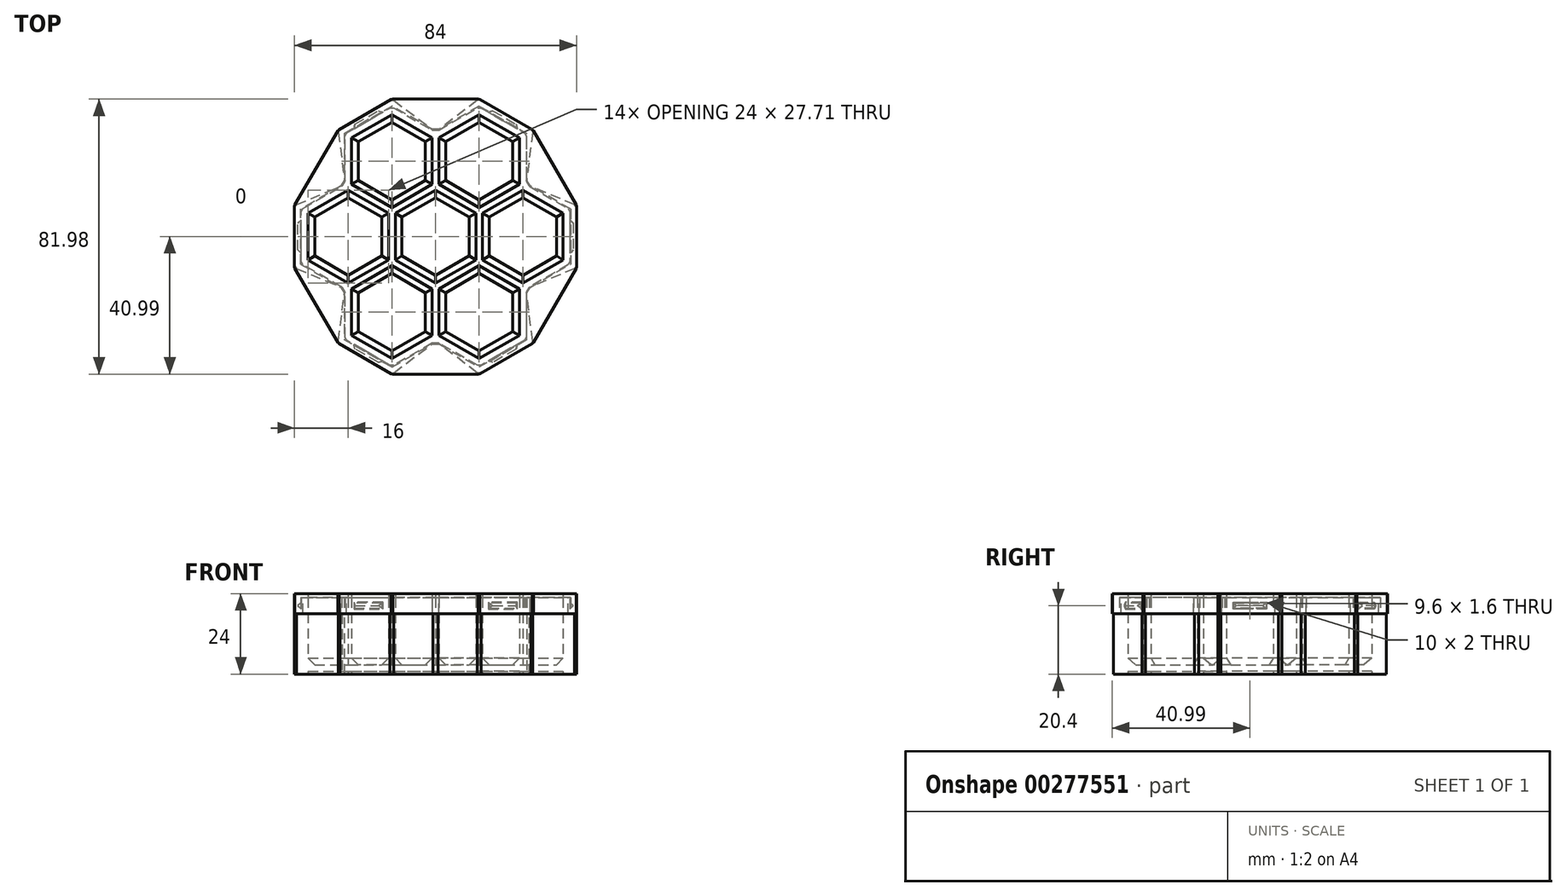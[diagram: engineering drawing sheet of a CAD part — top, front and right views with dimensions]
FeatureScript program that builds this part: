
annotation { "Feature Type Name" : "Feature", "Feature Type Description" : "" }
export const myFeature = defineFeature(function(context is Context, id is Id, definition is map)
    precondition{}
    {
        {
            assignVariable(context, id + "F0", {"name" : "BOX_HEIGHT", "anyValue" : 24});
        }
        {
            assignVariable(context, id + "F1", {"name" : "DICE_HEIGHT", "anyValue" : 20});
        }
        {
            assignVariable(context, id + "F2", {"name" : "LID_THICNESS", "anyValue" : 1.2});
        }
        {
            assignVariable(context, id + "F3", {"name" : "LID_HEIGHT", "anyValue" : 6});
        }
        {
            assignVariable(context, id + "F4", {"name" : "WALL_THICNESS", "anyValue" : 2});
        }
        {
            assignVariable(context, id + "F5", {"name" : "WALL_OVERLAP", "anyValue" : 2});
        }
        {
            var Q0;
            Q0=qCreatedBy(makeId("Top.planeOp"),FACE);
            var sketch = newSketch(context, id + "F6", { "sketchPlane" : qUnion([Q0])});
            skCircle(sketch, "E0.cCircle", {"center": v(0, 0) * mm, "radius": 12 * mm, "construction": true});
            skLineSegment(sketch, "E0.0", {"start": v(12, 6.93) * mm, "end": v(12, -6.93) * mm});
            skLineSegment(sketch, "E0.1", {"start": v(12, -6.93) * mm, "end": v(0, -13.86) * mm});
            skLineSegment(sketch, "E0.2", {"start": v(0, -13.86) * mm, "end": v(-12, -6.93) * mm});
            skLineSegment(sketch, "E0.3", {"start": v(-12, -6.93) * mm, "end": v(-12, 6.93) * mm});
            skLineSegment(sketch, "E0.4", {"start": v(-12, 6.93) * mm, "end": v(0, 13.86) * mm});
            skLineSegment(sketch, "E0.5", {"start": v(0, 13.86) * mm, "end": v(12, 6.93) * mm});
            skPoint(sketch, "E0.0.midPoint", {"position": v(12, 0) * mm});
            skSolve(sketch);
        }
        {
            var Q0;
            Q0=qCreatedBy(makeId("Top.planeOp"),FACE);
            var sketch = newSketch(context, id + "F7", { "sketchPlane" : qUnion([Q0])});
            skCircle(sketch, "E1.cCircle", {"center": v(26, 0) * mm, "radius": 12 * mm, "construction": true});
            skLineSegment(sketch, "E1.0", {"start": v(38, 6.93) * mm, "end": v(38, -6.93) * mm});
            skLineSegment(sketch, "E1.1", {"start": v(38, -6.93) * mm, "end": v(26, -13.86) * mm});
            skLineSegment(sketch, "E1.2", {"start": v(26, -13.86) * mm, "end": v(14, -6.93) * mm});
            skLineSegment(sketch, "E1.3", {"start": v(14, -6.93) * mm, "end": v(14, 6.93) * mm});
            skLineSegment(sketch, "E1.4", {"start": v(14, 6.93) * mm, "end": v(26, 13.86) * mm});
            skLineSegment(sketch, "E1.5", {"start": v(26, 13.86) * mm, "end": v(38, 6.93) * mm});
            skPoint(sketch, "E1.0.midPoint", {"position": v(38, 0) * mm});
            skLineSegment(sketch, "E2.1.0", {"start": v(13, 8.66) * mm, "end": v(1, 15.59) * mm});
            skLineSegment(sketch, "E2.1.1", {"start": v(1, 15.59) * mm, "end": v(1, 29.44) * mm});
            skLineSegment(sketch, "E2.1.2", {"start": v(1, 29.44) * mm, "end": v(13, 36.37) * mm});
            skLineSegment(sketch, "E2.1.3", {"start": v(13, 36.37) * mm, "end": v(25, 29.44) * mm});
            skPoint(sketch, "E2.1.4", {"position": v(19, 32.9) * mm});
            skLineSegment(sketch, "E2.1.5", {"start": v(25, 29.44) * mm, "end": v(25, 15.59) * mm});
            skLineSegment(sketch, "E2.1.6", {"start": v(25, 15.59) * mm, "end": v(13, 8.66) * mm});
            skLineSegment(sketch, "E2.2.0", {"start": v(-1, 15.59) * mm, "end": v(-13, 8.66) * mm});
            skLineSegment(sketch, "E2.2.1", {"start": v(-13, 8.66) * mm, "end": v(-25, 15.59) * mm});
            skLineSegment(sketch, "E2.2.2", {"start": v(-25, 15.59) * mm, "end": v(-25, 29.44) * mm});
            skLineSegment(sketch, "E2.2.3", {"start": v(-25, 29.44) * mm, "end": v(-13, 36.37) * mm});
            skPoint(sketch, "E2.2.4", {"position": v(-19, 32.9) * mm});
            skLineSegment(sketch, "E2.2.5", {"start": v(-13, 36.37) * mm, "end": v(-1, 29.44) * mm});
            skLineSegment(sketch, "E2.2.6", {"start": v(-1, 29.44) * mm, "end": v(-1, 15.59) * mm});
            skLineSegment(sketch, "E2.3.0", {"start": v(-14, 6.93) * mm, "end": v(-14, -6.93) * mm});
            skLineSegment(sketch, "E2.3.1", {"start": v(-14, -6.93) * mm, "end": v(-26, -13.86) * mm});
            skLineSegment(sketch, "E2.3.2", {"start": v(-26, -13.86) * mm, "end": v(-38, -6.93) * mm});
            skLineSegment(sketch, "E2.3.3", {"start": v(-38, -6.93) * mm, "end": v(-38, 6.93) * mm});
            skPoint(sketch, "E2.3.4", {"position": v(-38, 0) * mm});
            skLineSegment(sketch, "E2.3.5", {"start": v(-38, 6.93) * mm, "end": v(-26, 13.86) * mm});
            skLineSegment(sketch, "E2.3.6", {"start": v(-26, 13.86) * mm, "end": v(-14, 6.93) * mm});
            skLineSegment(sketch, "E2.4.0", {"start": v(-13, -8.66) * mm, "end": v(-1, -15.59) * mm});
            skLineSegment(sketch, "E2.4.1", {"start": v(-1, -15.59) * mm, "end": v(-1, -29.44) * mm});
            skLineSegment(sketch, "E2.4.2", {"start": v(-1, -29.44) * mm, "end": v(-13, -36.37) * mm});
            skLineSegment(sketch, "E2.4.3", {"start": v(-13, -36.37) * mm, "end": v(-25, -29.44) * mm});
            skPoint(sketch, "E2.4.4", {"position": v(-19, -32.9) * mm});
            skLineSegment(sketch, "E2.4.5", {"start": v(-25, -29.44) * mm, "end": v(-25, -15.59) * mm});
            skLineSegment(sketch, "E2.4.6", {"start": v(-25, -15.59) * mm, "end": v(-13, -8.66) * mm});
            skLineSegment(sketch, "E2.5.0", {"start": v(1, -15.59) * mm, "end": v(13, -8.66) * mm});
            skLineSegment(sketch, "E2.5.1", {"start": v(13, -8.66) * mm, "end": v(25, -15.59) * mm});
            skLineSegment(sketch, "E2.5.2", {"start": v(25, -15.59) * mm, "end": v(25, -29.44) * mm});
            skLineSegment(sketch, "E2.5.3", {"start": v(25, -29.44) * mm, "end": v(13, -36.37) * mm});
            skPoint(sketch, "E2.5.4", {"position": v(19, -32.9) * mm});
            skLineSegment(sketch, "E2.5.5", {"start": v(13, -36.37) * mm, "end": v(1, -29.44) * mm});
            skLineSegment(sketch, "E2.5.6", {"start": v(1, -29.44) * mm, "end": v(1, -15.59) * mm});
            skPoint(sketch, "E2.center", {"position": v(0, 0) * mm});
            skSolve(sketch);
        }
        {
            var Q0;
            Q0=qCreatedBy(makeId("Top.planeOp"),FACE);
            var sketch = newSketch(context, id + "F8", { "sketchPlane" : qUnion([Q0])});
            skLineSegment(sketch, "E3.0", {"start": v(-40, 8.08) * mm, "end": v(-27, 15.59) * mm});
            skLineSegment(sketch, "E3.1", {"start": v(-40, -8.08) * mm, "end": v(-40, 8.08) * mm});
            skLineSegment(sketch, "E3.2", {"start": v(-27, -15.59) * mm, "end": v(-40, -8.08) * mm});
            skLineSegment(sketch, "E4", {"start": v(-27, -15.59) * mm, "end": v(-12, -6.93) * mm, "construction": true});
            skLineSegment(sketch, "E5", {"start": v(-27, 15.59) * mm, "end": v(-12, 6.93) * mm, "construction": true});
            skLineSegment(sketch, "E6.1.0", {"start": v(0, -31.18) * mm, "end": v(-13, -38.68) * mm});
            skLineSegment(sketch, "E6.1.1", {"start": v(-13, -38.68) * mm, "end": v(-27, -30.6) * mm});
            skLineSegment(sketch, "E6.1.2", {"start": v(-27, -30.6) * mm, "end": v(-27, -15.59) * mm});
            skLineSegment(sketch, "E6.2.0", {"start": v(27, -15.59) * mm, "end": v(27, -30.6) * mm});
            skLineSegment(sketch, "E6.2.1", {"start": v(27, -30.6) * mm, "end": v(13, -38.68) * mm});
            skLineSegment(sketch, "E6.2.2", {"start": v(13, -38.68) * mm, "end": v(0, -31.18) * mm});
            skLineSegment(sketch, "E6.3.0", {"start": v(27, 15.59) * mm, "end": v(40, 8.08) * mm});
            skLineSegment(sketch, "E6.3.1", {"start": v(40, 8.08) * mm, "end": v(40, -8.08) * mm});
            skLineSegment(sketch, "E6.3.2", {"start": v(40, -8.08) * mm, "end": v(27, -15.59) * mm});
            skLineSegment(sketch, "E6.4.0", {"start": v(0, 31.18) * mm, "end": v(13, 38.68) * mm});
            skLineSegment(sketch, "E6.4.1", {"start": v(13, 38.68) * mm, "end": v(27, 30.6) * mm});
            skLineSegment(sketch, "E6.4.2", {"start": v(27, 30.6) * mm, "end": v(27, 15.59) * mm});
            skLineSegment(sketch, "E6.5.0", {"start": v(-27, 15.59) * mm, "end": v(-27, 30.6) * mm});
            skLineSegment(sketch, "E6.5.1", {"start": v(-27, 30.6) * mm, "end": v(-13, 38.68) * mm});
            skLineSegment(sketch, "E6.5.2", {"start": v(-13, 38.68) * mm, "end": v(0, 31.18) * mm});
            skPoint(sketch, "E6.center", {"position": v(0, 0) * mm});
            skSolve(sketch);
        }
        {
            var Q0;
            Q0=qCreatedBy(makeId("Top.planeOp"),FACE);
            var sketch = newSketch(context, id + "F9", { "sketchPlane" : qUnion([Q0])});
            skLineSegment(sketch, "E7.0", {"start": v(-42, -9.24) * mm, "end": v(-42, 9.24) * mm});
            skLineSegment(sketch, "E8", {"start": v(-42, 9.24) * mm, "end": v(-38, 6.93) * mm, "construction": true});
            skLineSegment(sketch, "E9", {"start": v(-42, -9.24) * mm, "end": v(-38, -6.93) * mm, "construction": true});
            skLineSegment(sketch, "E10", {"start": v(-42, -9.24) * mm, "end": v(-27, -15.59) * mm});
            skLineSegment(sketch, "E11", {"start": v(-42, 9.24) * mm, "end": v(-27, 15.59) * mm});
            skLineSegment(sketch, "E12.1.0", {"start": v(-13, -41) * mm, "end": v(0, -31.18) * mm});
            skLineSegment(sketch, "E12.1.1", {"start": v(-13, -41) * mm, "end": v(-29, -31.75) * mm});
            skLineSegment(sketch, "E12.1.2", {"start": v(-29, -31.75) * mm, "end": v(-27, -15.59) * mm});
            skLineSegment(sketch, "E12.2.0", {"start": v(29, -31.75) * mm, "end": v(27, -15.59) * mm});
            skLineSegment(sketch, "E12.2.1", {"start": v(29, -31.75) * mm, "end": v(13, -41) * mm});
            skLineSegment(sketch, "E12.2.2", {"start": v(13, -41) * mm, "end": v(0, -31.18) * mm});
            skLineSegment(sketch, "E12.3.0", {"start": v(42, 9.24) * mm, "end": v(27, 15.59) * mm});
            skLineSegment(sketch, "E12.3.1", {"start": v(42, 9.24) * mm, "end": v(42, -9.24) * mm});
            skLineSegment(sketch, "E12.3.2", {"start": v(42, -9.24) * mm, "end": v(27, -15.59) * mm});
            skLineSegment(sketch, "E12.4.0", {"start": v(13, 41) * mm, "end": v(0, 31.18) * mm});
            skLineSegment(sketch, "E12.4.1", {"start": v(13, 41) * mm, "end": v(29, 31.75) * mm});
            skLineSegment(sketch, "E12.4.2", {"start": v(29, 31.75) * mm, "end": v(27, 15.59) * mm});
            skLineSegment(sketch, "E12.5.0", {"start": v(-29, 31.75) * mm, "end": v(-27, 15.59) * mm});
            skLineSegment(sketch, "E12.5.1", {"start": v(-29, 31.75) * mm, "end": v(-13, 41) * mm});
            skLineSegment(sketch, "E12.5.2", {"start": v(-13, 41) * mm, "end": v(0, 31.18) * mm});
            skPoint(sketch, "E12.center", {"position": v(0, 0) * mm});
            skLineSegment(sketch, "E13", {"start": v(-29, 31.75) * mm, "end": v(-42, 9.24) * mm});
            skLineSegment(sketch, "E14", {"start": v(-42, -9.24) * mm, "end": v(-29, -31.75) * mm});
            skLineSegment(sketch, "E15", {"start": v(-13, -41) * mm, "end": v(13, -41) * mm});
            skLineSegment(sketch, "E16", {"start": v(29, -31.75) * mm, "end": v(42, -9.24) * mm});
            skLineSegment(sketch, "E17", {"start": v(42, 9.24) * mm, "end": v(29, 31.75) * mm});
            skLineSegment(sketch, "E18", {"start": v(13, 41) * mm, "end": v(-13, 41) * mm});
            skSolve(sketch);
        }
        {
            var Q0;
            Q0=makeQuery(id+"F8.imprint","IMPRINT",FACE,{"disambiguationData":[TD([[makeQuery(id+"F8.imprint","IMPRINT",EDGE,{"derivedFrom":sQuery(id+"F8.wireOp",EDGE,"E3.0")}),-1.0]])]});
            extrude(context, id + "F10", {"entities" : qUnion([Q0]), "depth" : (getVariable(context, 'BOX_HEIGHT') - getVariable(context, 'LID_THICNESS')) * mm});
        }
        {
            var Q0;
            Q0=makeQuery(id+"F9.imprint","IMPRINT",FACE,{"disambiguationData":[TD([[makeQuery(id+"F9.imprint","IMPRINT",EDGE,{"derivedFrom":sQuery(id+"F9.wireOp",EDGE,"E7.0")}),-1.0]])]});
            extrude(context, id + "F11", {"entities" : qUnion([Q0]), "operationType" : NewBodyOperationType.ADD, "depth" : (getVariable(context, 'BOX_HEIGHT') - getVariable(context, 'LID_HEIGHT')) * mm});
        }
        {
            var Q0;
            Q0=makeQuery(id+"F10.opExtrude","SWEPT_FACE",FACE,{"disambiguationData":[OSD([sQuery(id+"F8.wireOp",EDGE,"E6.3.1")])]});
            var sketch = newSketch(context, id + "F12", { "sketchPlane" : qUnion([Q0])});
            skLineSegment(sketch, "E19.bottom", {"start": v(5, 21.4) * mm, "end": v(-5, 21.4) * mm});
            skLineSegment(sketch, "E19.top", {"start": v(5, 19.4) * mm, "end": v(-5, 19.4) * mm});
            skLineSegment(sketch, "E19.left", {"start": v(5, 21.4) * mm, "end": v(5, 19.4) * mm});
            skLineSegment(sketch, "E19.right", {"start": v(-5, 21.4) * mm, "end": v(-5, 19.4) * mm});
            skPoint(sketch, "E19.middle", {"position": v(0, 20.4) * mm});
            skPoint(sketch, "E19.middle.positionSnap0", {"position": v(-8.08, 20.4) * mm});
            skPoint(sketch, "E19.centerSnap0", {"position": v(-8.08, 20.4) * mm});
            skSolve(sketch);
        }
        {
            var Q0;
            Q0=makeQuery(id+"F12.imprint","IMPRINT",FACE,{"disambiguationData":[TD([[makeQuery(id+"F12.imprint","IMPRINT",EDGE,{"derivedFrom":sQuery(id+"F12.wireOp",EDGE,"E19.bottom")}),1.0]])]});
            extrude(context, id + "F13", {"entities" : qUnion([Q0]), "depth" : 25 * mm, "hasDraft" : true, "draftAngle" : 45 * degree, "draftPullDirection" : true});
        }
        {
            var Q0;
            Q0=qCreatedBy(makeId("Front.planeOp"),FACE);
            var sketch = newSketch(context, id + "F14", { "sketchPlane" : qUnion([Q0])});
            skLineSegment(sketch, "E20", {"start": v(0, 0) * mm, "end": v(0, 24) * mm, "construction": true});
            skSolve(sketch);
        }
        {
            var Q0;
            Q0=makeQuery(id+"F13.opExtrude","SWEPT_BODY",BODY,{"disambiguationData":[OSD([sQuery(id+"F12.wireOp",EDGE,"E19.bottom"),sQuery(id+"F12.wireOp",EDGE,"E19.top"),sQuery(id+"F12.wireOp",EDGE,"E19.left"),sQuery(id+"F12.wireOp",EDGE,"E19.right")])]});
            var Q1;
            Q1=sQuery(id+"F14.wireOp",EDGE,"E20");
            circularPattern(context, id + "F15", {"operationType" : NewBodyOperationType.ADD, "entities" : qUnion([Q0]), "axis" : qUnion([Q1]), "angle" : 360 * degree, "instanceCount" : 6, "equalSpace" : true});
        }
        {
            var Q0;
            Q0=makeQuery(id+"F10.opExtrude","SWEPT_EDGE",EDGE,{"disambiguationData":[OSD([sQuery(id+"F8.wireOp",EDGE,"E6.3.0"),sQuery(id+"F8.wireOp",EDGE,"E6.4.2")])]});
            var Q1;
            Q1=makeQuery(id+"F10.opExtrude","SWEPT_EDGE",EDGE,{"disambiguationData":[OSD([sQuery(id+"F8.wireOp",EDGE,"E6.4.0"),sQuery(id+"F8.wireOp",EDGE,"E6.5.2")])]});
            var Q2;
            Q2=makeQuery(id+"F10.opExtrude","SWEPT_EDGE",EDGE,{"disambiguationData":[OSD([sQuery(id+"F8.wireOp",EDGE,"E3.0"),sQuery(id+"F8.wireOp",EDGE,"E6.5.0")])]});
            var Q3;
            Q3=makeQuery(id+"F10.opExtrude","SWEPT_EDGE",EDGE,{"disambiguationData":[OSD([sQuery(id+"F8.wireOp",EDGE,"E3.2"),sQuery(id+"F8.wireOp",EDGE,"E6.1.2")])]});
            var Q4;
            Q4=makeQuery(id+"F10.opExtrude","SWEPT_EDGE",EDGE,{"disambiguationData":[OSD([sQuery(id+"F8.wireOp",EDGE,"E6.1.0"),sQuery(id+"F8.wireOp",EDGE,"E6.2.2")])]});
            var Q5;
            Q5=makeQuery(id+"F10.opExtrude","SWEPT_EDGE",EDGE,{"disambiguationData":[OSD([sQuery(id+"F8.wireOp",EDGE,"E6.2.0"),sQuery(id+"F8.wireOp",EDGE,"E6.3.2")])]});
            chamfer(context, id + "F16", {"entities" : qUnion([Q0, Q1, Q2, Q3, Q4, Q5]), "width" : (getVariable(context, 'WALL_THICNESS')) * mm, "tangentPropagation" : true});
        }
        {
            var Q0;
            Q0=makeQuery(id+"F9.imprint","IMPRINT",FACE,{"disambiguationData":[TD([[makeQuery(id+"F9.imprint","IMPRINT",EDGE,{"derivedFrom":sQuery(id+"F9.wireOp",EDGE,"E7.0")}),-1.0]])]});
            var Q1;
            Q1=makeQuery(id+"F9.imprint","IMPRINT",FACE,{"disambiguationData":[TD([[makeQuery(id+"F9.imprint","IMPRINT",EDGE,{"derivedFrom":sQuery(id+"F9.wireOp",EDGE,"E11")}),1.0]])]});
            var Q2;
            Q2=makeQuery(id+"F9.imprint","IMPRINT",FACE,{"disambiguationData":[TD([[makeQuery(id+"F9.imprint","IMPRINT",EDGE,{"derivedFrom":sQuery(id+"F9.wireOp",EDGE,"E10")}),-1.0]])]});
            var Q3;
            Q3=makeQuery(id+"F9.imprint","IMPRINT",FACE,{"disambiguationData":[TD([[makeQuery(id+"F9.imprint","IMPRINT",EDGE,{"derivedFrom":sQuery(id+"F9.wireOp",EDGE,"E12.1.0")}),-1.0]])]});
            var Q4;
            Q4=makeQuery(id+"F9.imprint","IMPRINT",FACE,{"disambiguationData":[TD([[makeQuery(id+"F9.imprint","IMPRINT",EDGE,{"derivedFrom":sQuery(id+"F9.wireOp",EDGE,"E12.2.0")}),-1.0]])]});
            var Q5;
            Q5=makeQuery(id+"F9.imprint","IMPRINT",FACE,{"disambiguationData":[TD([[makeQuery(id+"F9.imprint","IMPRINT",EDGE,{"derivedFrom":sQuery(id+"F9.wireOp",EDGE,"E12.3.0")}),-1.0]])]});
            var Q6;
            Q6=makeQuery(id+"F9.imprint","IMPRINT",FACE,{"disambiguationData":[TD([[makeQuery(id+"F9.imprint","IMPRINT",EDGE,{"derivedFrom":sQuery(id+"F9.wireOp",EDGE,"E12.4.0")}),-1.0]])]});
            extrude(context, id + "F17", {"entities" : qUnion([Q0, Q1, Q2, Q3, Q4, Q5, Q6]), "depth" : (getVariable(context, 'BOX_HEIGHT')) * mm, "hasSecondDirection" : true, "secondDirectionOppositeDirection" : false, "secondDirectionDepth" : (getVariable(context, 'BOX_HEIGHT') - getVariable(context, 'LID_HEIGHT')) * mm});
        }
        {
            var Q0;
            Q0=makeQuery(id+"F10.opExtrude","SWEPT_BODY",BODY,{"disambiguationData":[OSD([sQuery(id+"F8.wireOp",EDGE,"E3.0"),sQuery(id+"F8.wireOp",EDGE,"E3.1"),sQuery(id+"F8.wireOp",EDGE,"E3.2"),sQuery(id+"F8.wireOp",EDGE,"E6.1.0"),sQuery(id+"F8.wireOp",EDGE,"E6.1.1"),sQuery(id+"F8.wireOp",EDGE,"E6.1.2"),sQuery(id+"F8.wireOp",EDGE,"E6.2.0"),sQuery(id+"F8.wireOp",EDGE,"E6.2.1"),sQuery(id+"F8.wireOp",EDGE,"E6.2.2"),sQuery(id+"F8.wireOp",EDGE,"E6.3.0"),sQuery(id+"F8.wireOp",EDGE,"E6.3.1"),sQuery(id+"F8.wireOp",EDGE,"E6.3.2"),sQuery(id+"F8.wireOp",EDGE,"E6.4.0"),sQuery(id+"F8.wireOp",EDGE,"E6.4.1"),sQuery(id+"F8.wireOp",EDGE,"E6.4.2"),sQuery(id+"F8.wireOp",EDGE,"E6.5.0"),sQuery(id+"F8.wireOp",EDGE,"E6.5.1"),sQuery(id+"F8.wireOp",EDGE,"E6.5.2")])]});
            var Q1;
            Q1=makeQuery(id+"F17.opExtrude","SWEPT_BODY",BODY,{"disambiguationData":[OSD([sQuery(id+"F9.wireOp",EDGE,"E7.0"),sQuery(id+"F9.wireOp",EDGE,"E12.1.1"),sQuery(id+"F9.wireOp",EDGE,"E12.2.1"),sQuery(id+"F9.wireOp",EDGE,"E12.3.1"),sQuery(id+"F9.wireOp",EDGE,"E12.4.1"),sQuery(id+"F9.wireOp",EDGE,"E12.5.1"),sQuery(id+"F9.wireOp",EDGE,"E13"),sQuery(id+"F9.wireOp",EDGE,"E14"),sQuery(id+"F9.wireOp",EDGE,"E15"),sQuery(id+"F9.wireOp",EDGE,"E16"),sQuery(id+"F9.wireOp",EDGE,"E17"),sQuery(id+"F9.wireOp",EDGE,"E18")])]});
            var Q2;
            Q2=makeQuery(id+"F10.opExtrude","SWEPT_FACE",FACE,{"disambiguationData":[OSD([sQuery(id+"F8.wireOp",EDGE,"E6.3.0")])]});
            var Q3;
            Q3=makeQuery(id+"F16.opChamfer","BLEND_FACE",FACE,{"disambiguationData":[OSD([sQuery(id+"F8.wireOp",EDGE,"E6.3.0"),sQuery(id+"F8.wireOp",EDGE,"E6.4.2")])]});
            var Q4;
            Q4=makeQuery(id+"F10.opExtrude","SWEPT_FACE",FACE,{"disambiguationData":[OSD([sQuery(id+"F8.wireOp",EDGE,"E6.4.2")])]});
            var Q5;
            Q5=makeQuery(id+"F10.opExtrude","SWEPT_FACE",FACE,{"disambiguationData":[OSD([sQuery(id+"F8.wireOp",EDGE,"E6.4.1")])]});
            var Q6;
            Q6=makeQuery(id+"F10.opExtrude","SWEPT_FACE",FACE,{"disambiguationData":[OSD([sQuery(id+"F8.wireOp",EDGE,"E6.4.0")])]});
            var Q7;
            Q7=makeQuery(id+"F16.opChamfer","BLEND_FACE",FACE,{"disambiguationData":[OSD([sQuery(id+"F8.wireOp",EDGE,"E6.4.0"),sQuery(id+"F8.wireOp",EDGE,"E6.5.2")])]});
            var Q8;
            Q8=makeQuery(id+"F10.opExtrude","SWEPT_FACE",FACE,{"disambiguationData":[OSD([sQuery(id+"F8.wireOp",EDGE,"E6.5.2")])]});
            var Q9;
            Q9=makeQuery(id+"F10.opExtrude","SWEPT_FACE",FACE,{"disambiguationData":[OSD([sQuery(id+"F8.wireOp",EDGE,"E6.5.1")])]});
            var Q10;
            Q10=makeQuery(id+"F10.opExtrude","SWEPT_FACE",FACE,{"disambiguationData":[OSD([sQuery(id+"F8.wireOp",EDGE,"E6.5.0")])]});
            var Q11;
            Q11=makeQuery(id+"F16.opChamfer","BLEND_FACE",FACE,{"disambiguationData":[OSD([sQuery(id+"F8.wireOp",EDGE,"E3.0"),sQuery(id+"F8.wireOp",EDGE,"E6.5.0")])]});
            var Q12;
            Q12=makeQuery(id+"F10.opExtrude","SWEPT_FACE",FACE,{"disambiguationData":[OSD([sQuery(id+"F8.wireOp",EDGE,"E3.0")])]});
            var Q13;
            Q13=makeQuery(id+"F10.opExtrude","SWEPT_FACE",FACE,{"disambiguationData":[OSD([sQuery(id+"F8.wireOp",EDGE,"E3.1")])]});
            var Q14;
            Q14=makeQuery(id+"F10.opExtrude","SWEPT_FACE",FACE,{"disambiguationData":[OSD([sQuery(id+"F8.wireOp",EDGE,"E3.2")])]});
            var Q15;
            Q15=makeQuery(id+"F16.opChamfer","BLEND_FACE",FACE,{"disambiguationData":[OSD([sQuery(id+"F8.wireOp",EDGE,"E3.2"),sQuery(id+"F8.wireOp",EDGE,"E6.1.2")])]});
            var Q16;
            Q16=makeQuery(id+"F10.opExtrude","SWEPT_FACE",FACE,{"disambiguationData":[OSD([sQuery(id+"F8.wireOp",EDGE,"E6.1.2")])]});
            var Q17;
            Q17=makeQuery(id+"F10.opExtrude","SWEPT_FACE",FACE,{"disambiguationData":[OSD([sQuery(id+"F8.wireOp",EDGE,"E6.1.1")])]});
            var Q18;
            Q18=makeQuery(id+"F10.opExtrude","SWEPT_FACE",FACE,{"disambiguationData":[OSD([sQuery(id+"F8.wireOp",EDGE,"E6.1.0")])]});
            var Q19;
            Q19=makeQuery(id+"F16.opChamfer","BLEND_FACE",FACE,{"disambiguationData":[OSD([sQuery(id+"F8.wireOp",EDGE,"E6.1.0"),sQuery(id+"F8.wireOp",EDGE,"E6.2.2")])]});
            var Q20;
            Q20=makeQuery(id+"F10.opExtrude","SWEPT_FACE",FACE,{"disambiguationData":[OSD([sQuery(id+"F8.wireOp",EDGE,"E6.2.2")])]});
            var Q21;
            Q21=makeQuery(id+"F10.opExtrude","SWEPT_FACE",FACE,{"disambiguationData":[OSD([sQuery(id+"F8.wireOp",EDGE,"E6.2.1")])]});
            var Q22;
            Q22=makeQuery(id+"F10.opExtrude","SWEPT_FACE",FACE,{"disambiguationData":[OSD([sQuery(id+"F8.wireOp",EDGE,"E6.2.0")])]});
            var Q23;
            Q23=makeQuery(id+"F16.opChamfer","BLEND_FACE",FACE,{"disambiguationData":[OSD([sQuery(id+"F8.wireOp",EDGE,"E6.2.0"),sQuery(id+"F8.wireOp",EDGE,"E6.3.2")])]});
            var Q24;
            Q24=makeQuery(id+"F10.opExtrude","SWEPT_FACE",FACE,{"disambiguationData":[OSD([sQuery(id+"F8.wireOp",EDGE,"E6.3.2")])]});
            var Q25;
            Q25=makeQuery(id+"F10.opExtrude","SWEPT_FACE",FACE,{"disambiguationData":[OSD([sQuery(id+"F8.wireOp",EDGE,"E6.3.1")])]});
            booleanBodies(context, id + "F18", {"operationType" : BooleanOperationType.SUBTRACTION, "tools" : qUnion([Q0]), "targets" : qUnion([Q1]), "offset" : true, "entitiesToOffset" : qUnion([Q2, Q3, Q4, Q5, Q6, Q7, Q8, Q9, Q10, Q11, Q12, Q13, Q14, Q15, Q16, Q17, Q18, Q19, Q20, Q21, Q22, Q23, Q24, Q25]), "offsetDistance" : 0.2 * mm, "keepTools" : true});
        }
        {
            var Q0;
            Q0=makeQuery(id+"F7.imprint","IMPRINT",FACE,{"disambiguationData":[TD([[makeQuery(id+"F7.imprint","IMPRINT",EDGE,{"derivedFrom":sQuery(id+"F7.wireOp",EDGE,"E2.4.0")}),-1.0]])]});
            var Q1;
            Q1=makeQuery(id+"F7.imprint","IMPRINT",FACE,{"disambiguationData":[TD([[makeQuery(id+"F7.imprint","IMPRINT",EDGE,{"derivedFrom":sQuery(id+"F7.wireOp",EDGE,"E2.5.0")}),-1.0]])]});
            var Q2;
            Q2=makeQuery(id+"F7.imprint","IMPRINT",FACE,{"disambiguationData":[TD([[makeQuery(id+"F7.imprint","IMPRINT",EDGE,{"derivedFrom":sQuery(id+"F7.wireOp",EDGE,"E1.0")}),-1.0]])]});
            var Q3;
            Q3=makeQuery(id+"F6.imprint","IMPRINT",FACE,{"disambiguationData":[TD([[makeQuery(id+"F6.imprint","IMPRINT",EDGE,{"derivedFrom":sQuery(id+"F6.wireOp",EDGE,"E0.0")}),-1.0]])]});
            var Q4;
            Q4=makeQuery(id+"F7.imprint","IMPRINT",FACE,{"disambiguationData":[TD([[makeQuery(id+"F7.imprint","IMPRINT",EDGE,{"derivedFrom":sQuery(id+"F7.wireOp",EDGE,"E2.3.0")}),-1.0]])]});
            var Q5;
            Q5=makeQuery(id+"F7.imprint","IMPRINT",FACE,{"disambiguationData":[TD([[makeQuery(id+"F7.imprint","IMPRINT",EDGE,{"derivedFrom":sQuery(id+"F7.wireOp",EDGE,"E2.2.0")}),-1.0]])]});
            var Q6;
            Q6=makeQuery(id+"F7.imprint","IMPRINT",FACE,{"disambiguationData":[TD([[makeQuery(id+"F7.imprint","IMPRINT",EDGE,{"derivedFrom":sQuery(id+"F7.wireOp",EDGE,"E2.1.0")}),-1.0]])]});
            extrude(context, id + "F19", {"entities" : qUnion([Q0, Q1, Q2, Q3, Q4, Q5, Q6]), "operationType" : NewBodyOperationType.REMOVE, "endBound" : BoundingType.THROUGH_ALL, "depth" : 25 * mm, "hasSecondDirection" : true, "secondDirectionOppositeDirection" : false, "secondDirectionDepth" : (getVariable(context, 'BOX_HEIGHT') - getVariable(context, 'DICE_HEIGHT') - getVariable(context, 'LID_THICNESS')) * mm});
        }
        {
            var Q0;
            Q0=makeQuery(id+"F19.boolean.opBoolean","COPY",EDGE,{"derivedFrom":makeQuery(id+"F19.opExtrude","CAP_EDGE",EDGE,{"disambiguationData":[OSD([sQuery(id+"F7.wireOp",EDGE,"E2.4.3")])],"isStart":true})});
            var Q1;
            Q1=makeQuery(id+"F19.boolean.opBoolean","COPY",EDGE,{"derivedFrom":makeQuery(id+"F19.opExtrude","CAP_EDGE",EDGE,{"disambiguationData":[OSD([sQuery(id+"F7.wireOp",EDGE,"E2.4.5")])],"isStart":true})});
            var Q2;
            Q2=makeQuery(id+"F19.boolean.opBoolean","COPY",EDGE,{"derivedFrom":makeQuery(id+"F19.opExtrude","CAP_EDGE",EDGE,{"disambiguationData":[OSD([sQuery(id+"F7.wireOp",EDGE,"E2.4.6")])],"isStart":true})});
            var Q3;
            Q3=makeQuery(id+"F19.boolean.opBoolean","COPY",EDGE,{"derivedFrom":makeQuery(id+"F19.opExtrude","CAP_EDGE",EDGE,{"disambiguationData":[OSD([sQuery(id+"F7.wireOp",EDGE,"E2.4.0")])],"isStart":true})});
            var Q4;
            Q4=makeQuery(id+"F19.boolean.opBoolean","COPY",EDGE,{"derivedFrom":makeQuery(id+"F19.opExtrude","CAP_EDGE",EDGE,{"disambiguationData":[OSD([sQuery(id+"F7.wireOp",EDGE,"E2.4.2")])],"isStart":true})});
            var Q5;
            Q5=makeQuery(id+"F19.boolean.opBoolean","COPY",EDGE,{"derivedFrom":makeQuery(id+"F19.opExtrude","CAP_EDGE",EDGE,{"disambiguationData":[OSD([sQuery(id+"F7.wireOp",EDGE,"E2.4.1")])],"isStart":true})});
            var Q6;
            Q6=makeQuery(id+"F19.boolean.opBoolean","COPY",EDGE,{"derivedFrom":makeQuery(id+"F19.opExtrude","CAP_EDGE",EDGE,{"disambiguationData":[OSD([sQuery(id+"F7.wireOp",EDGE,"E2.3.1")])],"isStart":true})});
            var Q7;
            Q7=makeQuery(id+"F19.boolean.opBoolean","COPY",EDGE,{"derivedFrom":makeQuery(id+"F19.opExtrude","CAP_EDGE",EDGE,{"disambiguationData":[OSD([sQuery(id+"F7.wireOp",EDGE,"E2.3.0")])],"isStart":true})});
            var Q8;
            Q8=makeQuery(id+"F19.boolean.opBoolean","COPY",EDGE,{"derivedFrom":makeQuery(id+"F19.opExtrude","CAP_EDGE",EDGE,{"disambiguationData":[OSD([sQuery(id+"F7.wireOp",EDGE,"E2.2.0")])],"isStart":true})});
            var Q9;
            Q9=makeQuery(id+"F19.boolean.opBoolean","COPY",EDGE,{"derivedFrom":makeQuery(id+"F19.opExtrude","CAP_EDGE",EDGE,{"disambiguationData":[OSD([sQuery(id+"F7.wireOp",EDGE,"E2.2.6")])],"isStart":true})});
            var Q10;
            Q10=makeQuery(id+"F19.boolean.opBoolean","COPY",EDGE,{"derivedFrom":makeQuery(id+"F19.opExtrude","CAP_EDGE",EDGE,{"disambiguationData":[OSD([sQuery(id+"F6.wireOp",EDGE,"E0.1")])],"isStart":true})});
            var Q11;
            Q11=makeQuery(id+"F19.boolean.opBoolean","COPY",EDGE,{"derivedFrom":makeQuery(id+"F19.opExtrude","CAP_EDGE",EDGE,{"disambiguationData":[OSD([sQuery(id+"F6.wireOp",EDGE,"E0.0")])],"isStart":true})});
            var Q12;
            Q12=makeQuery(id+"F19.boolean.opBoolean","COPY",EDGE,{"derivedFrom":makeQuery(id+"F19.opExtrude","CAP_EDGE",EDGE,{"disambiguationData":[OSD([sQuery(id+"F7.wireOp",EDGE,"E2.1.6")])],"isStart":true})});
            var Q13;
            Q13=makeQuery(id+"F19.boolean.opBoolean","COPY",EDGE,{"derivedFrom":makeQuery(id+"F19.opExtrude","CAP_EDGE",EDGE,{"disambiguationData":[OSD([sQuery(id+"F7.wireOp",EDGE,"E2.1.5")])],"isStart":true})});
            var Q14;
            Q14=makeQuery(id+"F19.boolean.opBoolean","COPY",EDGE,{"derivedFrom":makeQuery(id+"F19.opExtrude","CAP_EDGE",EDGE,{"disambiguationData":[OSD([sQuery(id+"F7.wireOp",EDGE,"E1.1")])],"isStart":true})});
            var Q15;
            Q15=makeQuery(id+"F19.boolean.opBoolean","COPY",EDGE,{"derivedFrom":makeQuery(id+"F19.opExtrude","CAP_EDGE",EDGE,{"disambiguationData":[OSD([sQuery(id+"F7.wireOp",EDGE,"E1.0")])],"isStart":true})});
            var Q16;
            Q16=makeQuery(id+"F19.boolean.opBoolean","COPY",EDGE,{"derivedFrom":makeQuery(id+"F19.opExtrude","CAP_EDGE",EDGE,{"disambiguationData":[OSD([sQuery(id+"F7.wireOp",EDGE,"E2.5.3")])],"isStart":true})});
            var Q17;
            Q17=makeQuery(id+"F19.boolean.opBoolean","COPY",EDGE,{"derivedFrom":makeQuery(id+"F19.opExtrude","CAP_EDGE",EDGE,{"disambiguationData":[OSD([sQuery(id+"F7.wireOp",EDGE,"E2.5.2")])],"isStart":true})});
            var Q18;
            Q18=makeQuery(id+"F19.boolean.opBoolean","COPY",EDGE,{"derivedFrom":makeQuery(id+"F19.opExtrude","CAP_EDGE",EDGE,{"disambiguationData":[OSD([sQuery(id+"F7.wireOp",EDGE,"E2.3.2")])],"isStart":true})});
            var Q19;
            Q19=makeQuery(id+"F19.boolean.opBoolean","COPY",EDGE,{"derivedFrom":makeQuery(id+"F19.opExtrude","CAP_EDGE",EDGE,{"disambiguationData":[OSD([sQuery(id+"F7.wireOp",EDGE,"E2.3.3")])],"isStart":true})});
            var Q20;
            Q20=makeQuery(id+"F19.boolean.opBoolean","COPY",EDGE,{"derivedFrom":makeQuery(id+"F19.opExtrude","CAP_EDGE",EDGE,{"disambiguationData":[OSD([sQuery(id+"F7.wireOp",EDGE,"E2.2.1")])],"isStart":true})});
            var Q21;
            Q21=makeQuery(id+"F19.boolean.opBoolean","COPY",EDGE,{"derivedFrom":makeQuery(id+"F19.opExtrude","CAP_EDGE",EDGE,{"disambiguationData":[OSD([sQuery(id+"F7.wireOp",EDGE,"E2.2.2")])],"isStart":true})});
            var Q22;
            Q22=makeQuery(id+"F19.boolean.opBoolean","COPY",EDGE,{"derivedFrom":makeQuery(id+"F19.opExtrude","CAP_EDGE",EDGE,{"disambiguationData":[OSD([sQuery(id+"F6.wireOp",EDGE,"E0.2")])],"isStart":true})});
            var Q23;
            Q23=makeQuery(id+"F19.boolean.opBoolean","COPY",EDGE,{"derivedFrom":makeQuery(id+"F19.opExtrude","CAP_EDGE",EDGE,{"disambiguationData":[OSD([sQuery(id+"F6.wireOp",EDGE,"E0.3")])],"isStart":true})});
            var Q24;
            Q24=makeQuery(id+"F19.boolean.opBoolean","COPY",EDGE,{"derivedFrom":makeQuery(id+"F19.opExtrude","CAP_EDGE",EDGE,{"disambiguationData":[OSD([sQuery(id+"F7.wireOp",EDGE,"E2.1.0")])],"isStart":true})});
            var Q25;
            Q25=makeQuery(id+"F19.boolean.opBoolean","COPY",EDGE,{"derivedFrom":makeQuery(id+"F19.opExtrude","CAP_EDGE",EDGE,{"disambiguationData":[OSD([sQuery(id+"F7.wireOp",EDGE,"E2.1.1")])],"isStart":true})});
            var Q26;
            Q26=makeQuery(id+"F19.boolean.opBoolean","COPY",EDGE,{"derivedFrom":makeQuery(id+"F19.opExtrude","CAP_EDGE",EDGE,{"disambiguationData":[OSD([sQuery(id+"F7.wireOp",EDGE,"E1.2")])],"isStart":true})});
            var Q27;
            Q27=makeQuery(id+"F19.boolean.opBoolean","COPY",EDGE,{"derivedFrom":makeQuery(id+"F19.opExtrude","CAP_EDGE",EDGE,{"disambiguationData":[OSD([sQuery(id+"F7.wireOp",EDGE,"E1.3")])],"isStart":true})});
            var Q28;
            Q28=makeQuery(id+"F19.boolean.opBoolean","COPY",EDGE,{"derivedFrom":makeQuery(id+"F19.opExtrude","CAP_EDGE",EDGE,{"disambiguationData":[OSD([sQuery(id+"F7.wireOp",EDGE,"E2.5.5")])],"isStart":true})});
            var Q29;
            Q29=makeQuery(id+"F19.boolean.opBoolean","COPY",EDGE,{"derivedFrom":makeQuery(id+"F19.opExtrude","CAP_EDGE",EDGE,{"disambiguationData":[OSD([sQuery(id+"F7.wireOp",EDGE,"E2.5.6")])],"isStart":true})});
            var Q30;
            Q30=makeQuery(id+"F19.boolean.opBoolean","COPY",EDGE,{"derivedFrom":makeQuery(id+"F19.opExtrude","CAP_EDGE",EDGE,{"disambiguationData":[OSD([sQuery(id+"F7.wireOp",EDGE,"E2.5.0")])],"isStart":true})});
            var Q31;
            Q31=makeQuery(id+"F19.boolean.opBoolean","COPY",EDGE,{"derivedFrom":makeQuery(id+"F19.opExtrude","CAP_EDGE",EDGE,{"disambiguationData":[OSD([sQuery(id+"F7.wireOp",EDGE,"E2.5.1")])],"isStart":true})});
            var Q32;
            Q32=makeQuery(id+"F19.boolean.opBoolean","COPY",EDGE,{"derivedFrom":makeQuery(id+"F19.opExtrude","CAP_EDGE",EDGE,{"disambiguationData":[OSD([sQuery(id+"F6.wireOp",EDGE,"E0.4")])],"isStart":true})});
            var Q33;
            Q33=makeQuery(id+"F19.boolean.opBoolean","COPY",EDGE,{"derivedFrom":makeQuery(id+"F19.opExtrude","CAP_EDGE",EDGE,{"disambiguationData":[OSD([sQuery(id+"F6.wireOp",EDGE,"E0.5")])],"isStart":true})});
            var Q34;
            Q34=makeQuery(id+"F19.boolean.opBoolean","COPY",EDGE,{"derivedFrom":makeQuery(id+"F19.opExtrude","CAP_EDGE",EDGE,{"disambiguationData":[OSD([sQuery(id+"F7.wireOp",EDGE,"E2.3.6")])],"isStart":true})});
            var Q35;
            Q35=makeQuery(id+"F19.boolean.opBoolean","COPY",EDGE,{"derivedFrom":makeQuery(id+"F19.opExtrude","CAP_EDGE",EDGE,{"disambiguationData":[OSD([sQuery(id+"F7.wireOp",EDGE,"E2.3.5")])],"isStart":true})});
            var Q36;
            Q36=makeQuery(id+"F19.boolean.opBoolean","COPY",EDGE,{"derivedFrom":makeQuery(id+"F19.opExtrude","CAP_EDGE",EDGE,{"disambiguationData":[OSD([sQuery(id+"F7.wireOp",EDGE,"E2.2.3")])],"isStart":true})});
            var Q37;
            Q37=makeQuery(id+"F19.boolean.opBoolean","COPY",EDGE,{"derivedFrom":makeQuery(id+"F19.opExtrude","CAP_EDGE",EDGE,{"disambiguationData":[OSD([sQuery(id+"F7.wireOp",EDGE,"E2.2.5")])],"isStart":true})});
            var Q38;
            Q38=makeQuery(id+"F19.boolean.opBoolean","COPY",EDGE,{"derivedFrom":makeQuery(id+"F19.opExtrude","CAP_EDGE",EDGE,{"disambiguationData":[OSD([sQuery(id+"F7.wireOp",EDGE,"E2.1.2")])],"isStart":true})});
            var Q39;
            Q39=makeQuery(id+"F19.boolean.opBoolean","COPY",EDGE,{"derivedFrom":makeQuery(id+"F19.opExtrude","CAP_EDGE",EDGE,{"disambiguationData":[OSD([sQuery(id+"F7.wireOp",EDGE,"E2.1.3")])],"isStart":true})});
            var Q40;
            Q40=makeQuery(id+"F19.boolean.opBoolean","COPY",EDGE,{"derivedFrom":makeQuery(id+"F19.opExtrude","CAP_EDGE",EDGE,{"disambiguationData":[OSD([sQuery(id+"F7.wireOp",EDGE,"E1.5")])],"isStart":true})});
            var Q41;
            Q41=makeQuery(id+"F19.boolean.opBoolean","COPY",EDGE,{"derivedFrom":makeQuery(id+"F19.opExtrude","CAP_EDGE",EDGE,{"disambiguationData":[OSD([sQuery(id+"F7.wireOp",EDGE,"E1.4")])],"isStart":true})});
            chamfer(context, id + "F20", {"entities" : qUnion([Q0, Q1, Q2, Q3, Q4, Q5, Q6, Q7, Q8, Q9, Q10, Q11, Q12, Q13, Q14, Q15, Q16, Q17, Q18, Q19, Q20, Q21, Q22, Q23, Q24, Q25, Q26, Q27, Q28, Q29, Q30, Q31, Q32, Q33, Q34, Q35, Q36, Q37, Q38, Q39, Q40, Q41]), "width" : (getVariable(context, 'WALL_THICNESS')) * mm, "tangentPropagation" : true});
        }
        {
            var Q0;
            Q0=makeQuery(id+"F17.opExtrude","SWEPT_EDGE",EDGE,{"disambiguationData":[OSD([sQuery(id+"F9.wireOp",EDGE,"E7.0"),sQuery(id+"F9.wireOp",EDGE,"E10"),sQuery(id+"F9.wireOp",EDGE,"E14")])]});
            var Q1;
            Q1=makeQuery(id+"F11.opExtrude","SWEPT_EDGE",EDGE,{"disambiguationData":[OSD([sQuery(id+"F9.wireOp",EDGE,"E7.0"),sQuery(id+"F9.wireOp",EDGE,"E10"),sQuery(id+"F9.wireOp",EDGE,"E14")])]});
            var Q2;
            Q2=makeQuery(id+"F11.opExtrude","SWEPT_EDGE",EDGE,{"disambiguationData":[OSD([sQuery(id+"F9.wireOp",EDGE,"E12.1.1"),sQuery(id+"F9.wireOp",EDGE,"E12.1.2"),sQuery(id+"F9.wireOp",EDGE,"E14")])]});
            var Q3;
            Q3=makeQuery(id+"F11.opExtrude","SWEPT_EDGE",EDGE,{"disambiguationData":[OSD([sQuery(id+"F9.wireOp",EDGE,"E12.1.0"),sQuery(id+"F9.wireOp",EDGE,"E12.1.1"),sQuery(id+"F9.wireOp",EDGE,"E15")])]});
            var Q4;
            Q4=makeQuery(id+"F17.opExtrude","SWEPT_EDGE",EDGE,{"disambiguationData":[OSD([sQuery(id+"F9.wireOp",EDGE,"E12.1.1"),sQuery(id+"F9.wireOp",EDGE,"E12.1.2"),sQuery(id+"F9.wireOp",EDGE,"E14")])]});
            var Q5;
            Q5=makeQuery(id+"F17.opExtrude","SWEPT_EDGE",EDGE,{"disambiguationData":[OSD([sQuery(id+"F9.wireOp",EDGE,"E12.1.0"),sQuery(id+"F9.wireOp",EDGE,"E12.1.1"),sQuery(id+"F9.wireOp",EDGE,"E15")])]});
            var Q6;
            Q6=makeQuery(id+"F17.opExtrude","SWEPT_EDGE",EDGE,{"disambiguationData":[OSD([sQuery(id+"F9.wireOp",EDGE,"E7.0"),sQuery(id+"F9.wireOp",EDGE,"E11"),sQuery(id+"F9.wireOp",EDGE,"E13")])]});
            var Q7;
            Q7=makeQuery(id+"F11.opExtrude","SWEPT_EDGE",EDGE,{"disambiguationData":[OSD([sQuery(id+"F9.wireOp",EDGE,"E7.0"),sQuery(id+"F9.wireOp",EDGE,"E11"),sQuery(id+"F9.wireOp",EDGE,"E13")])]});
            var Q8;
            Q8=makeQuery(id+"F17.opExtrude","SWEPT_EDGE",EDGE,{"disambiguationData":[OSD([sQuery(id+"F9.wireOp",EDGE,"E12.2.1"),sQuery(id+"F9.wireOp",EDGE,"E12.2.2"),sQuery(id+"F9.wireOp",EDGE,"E15")])]});
            var Q9;
            Q9=makeQuery(id+"F11.opExtrude","SWEPT_EDGE",EDGE,{"disambiguationData":[OSD([sQuery(id+"F9.wireOp",EDGE,"E12.2.1"),sQuery(id+"F9.wireOp",EDGE,"E12.2.2"),sQuery(id+"F9.wireOp",EDGE,"E15")])]});
            var Q10;
            Q10=makeQuery(id+"F11.opExtrude","SWEPT_EDGE",EDGE,{"disambiguationData":[OSD([sQuery(id+"F9.wireOp",EDGE,"E12.2.0"),sQuery(id+"F9.wireOp",EDGE,"E12.2.1"),sQuery(id+"F9.wireOp",EDGE,"E16")])]});
            var Q11;
            Q11=makeQuery(id+"F17.opExtrude","SWEPT_EDGE",EDGE,{"disambiguationData":[OSD([sQuery(id+"F9.wireOp",EDGE,"E12.2.0"),sQuery(id+"F9.wireOp",EDGE,"E12.2.1"),sQuery(id+"F9.wireOp",EDGE,"E16")])]});
            var Q12;
            Q12=makeQuery(id+"F11.opExtrude","SWEPT_EDGE",EDGE,{"disambiguationData":[OSD([sQuery(id+"F9.wireOp",EDGE,"E12.3.1"),sQuery(id+"F9.wireOp",EDGE,"E12.3.2"),sQuery(id+"F9.wireOp",EDGE,"E16")])]});
            var Q13;
            Q13=makeQuery(id+"F17.opExtrude","SWEPT_EDGE",EDGE,{"disambiguationData":[OSD([sQuery(id+"F9.wireOp",EDGE,"E12.3.1"),sQuery(id+"F9.wireOp",EDGE,"E12.3.2"),sQuery(id+"F9.wireOp",EDGE,"E16")])]});
            var Q14;
            Q14=makeQuery(id+"F17.opExtrude","SWEPT_EDGE",EDGE,{"disambiguationData":[OSD([sQuery(id+"F9.wireOp",EDGE,"E12.3.0"),sQuery(id+"F9.wireOp",EDGE,"E12.3.1"),sQuery(id+"F9.wireOp",EDGE,"E17")])]});
            var Q15;
            Q15=makeQuery(id+"F11.opExtrude","SWEPT_EDGE",EDGE,{"disambiguationData":[OSD([sQuery(id+"F9.wireOp",EDGE,"E12.3.0"),sQuery(id+"F9.wireOp",EDGE,"E12.3.1"),sQuery(id+"F9.wireOp",EDGE,"E17")])]});
            var Q16;
            Q16=makeQuery(id+"F17.opExtrude","SWEPT_EDGE",EDGE,{"disambiguationData":[OSD([sQuery(id+"F9.wireOp",EDGE,"E12.4.1"),sQuery(id+"F9.wireOp",EDGE,"E12.4.2"),sQuery(id+"F9.wireOp",EDGE,"E17")])]});
            var Q17;
            Q17=makeQuery(id+"F11.opExtrude","SWEPT_EDGE",EDGE,{"disambiguationData":[OSD([sQuery(id+"F9.wireOp",EDGE,"E12.4.1"),sQuery(id+"F9.wireOp",EDGE,"E12.4.2"),sQuery(id+"F9.wireOp",EDGE,"E17")])]});
            var Q18;
            Q18=makeQuery(id+"F17.opExtrude","SWEPT_EDGE",EDGE,{"disambiguationData":[OSD([sQuery(id+"F9.wireOp",EDGE,"E12.4.0"),sQuery(id+"F9.wireOp",EDGE,"E12.4.1"),sQuery(id+"F9.wireOp",EDGE,"E18")])]});
            var Q19;
            Q19=makeQuery(id+"F11.opExtrude","SWEPT_EDGE",EDGE,{"disambiguationData":[OSD([sQuery(id+"F9.wireOp",EDGE,"E12.4.0"),sQuery(id+"F9.wireOp",EDGE,"E12.4.1"),sQuery(id+"F9.wireOp",EDGE,"E18")])]});
            var Q20;
            Q20=makeQuery(id+"F17.opExtrude","SWEPT_EDGE",EDGE,{"disambiguationData":[OSD([sQuery(id+"F9.wireOp",EDGE,"E12.5.1"),sQuery(id+"F9.wireOp",EDGE,"E12.5.2"),sQuery(id+"F9.wireOp",EDGE,"E18")])]});
            var Q21;
            Q21=makeQuery(id+"F11.opExtrude","SWEPT_EDGE",EDGE,{"disambiguationData":[OSD([sQuery(id+"F9.wireOp",EDGE,"E12.5.1"),sQuery(id+"F9.wireOp",EDGE,"E12.5.2"),sQuery(id+"F9.wireOp",EDGE,"E18")])]});
            var Q22;
            Q22=makeQuery(id+"F17.opExtrude","SWEPT_EDGE",EDGE,{"disambiguationData":[OSD([sQuery(id+"F9.wireOp",EDGE,"E12.5.0"),sQuery(id+"F9.wireOp",EDGE,"E12.5.1"),sQuery(id+"F9.wireOp",EDGE,"E13")])]});
            var Q23;
            Q23=makeQuery(id+"F11.opExtrude","SWEPT_EDGE",EDGE,{"disambiguationData":[OSD([sQuery(id+"F9.wireOp",EDGE,"E12.5.0"),sQuery(id+"F9.wireOp",EDGE,"E12.5.1"),sQuery(id+"F9.wireOp",EDGE,"E13")])]});
            var Q24;
            Q24=makeQuery(id+"F10.opExtrude","SWEPT_EDGE",EDGE,{"disambiguationData":[OSD([sQuery(id+"F8.wireOp",EDGE,"E6.5.0"),sQuery(id+"F8.wireOp",EDGE,"E6.5.1")])]});
            var Q25;
            Q25=makeQuery(id+"F10.opExtrude","SWEPT_EDGE",EDGE,{"disambiguationData":[OSD([sQuery(id+"F8.wireOp",EDGE,"E3.0"),sQuery(id+"F8.wireOp",EDGE,"E3.1")])]});
            var Q26;
            Q26=makeQuery(id+"F10.opExtrude","SWEPT_EDGE",EDGE,{"disambiguationData":[OSD([sQuery(id+"F8.wireOp",EDGE,"E3.1"),sQuery(id+"F8.wireOp",EDGE,"E3.2")])]});
            var Q27;
            Q27=makeQuery(id+"F10.opExtrude","SWEPT_EDGE",EDGE,{"disambiguationData":[OSD([sQuery(id+"F8.wireOp",EDGE,"E6.1.1"),sQuery(id+"F8.wireOp",EDGE,"E6.1.2")])]});
            var Q28;
            Q28=makeQuery(id+"F10.opExtrude","SWEPT_EDGE",EDGE,{"disambiguationData":[OSD([sQuery(id+"F8.wireOp",EDGE,"E6.1.0"),sQuery(id+"F8.wireOp",EDGE,"E6.1.1")])]});
            var Q29;
            Q29=makeQuery(id+"F10.opExtrude","SWEPT_EDGE",EDGE,{"disambiguationData":[OSD([sQuery(id+"F8.wireOp",EDGE,"E6.5.1"),sQuery(id+"F8.wireOp",EDGE,"E6.5.2")])]});
            var Q30;
            Q30=makeQuery(id+"F10.opExtrude","SWEPT_EDGE",EDGE,{"disambiguationData":[OSD([sQuery(id+"F8.wireOp",EDGE,"E6.4.0"),sQuery(id+"F8.wireOp",EDGE,"E6.4.1")])]});
            var Q31;
            Q31=makeQuery(id+"F10.opExtrude","SWEPT_EDGE",EDGE,{"disambiguationData":[OSD([sQuery(id+"F8.wireOp",EDGE,"E6.2.1"),sQuery(id+"F8.wireOp",EDGE,"E6.2.2")])]});
            var Q32;
            Q32=makeQuery(id+"F10.opExtrude","SWEPT_EDGE",EDGE,{"disambiguationData":[OSD([sQuery(id+"F8.wireOp",EDGE,"E6.3.0"),sQuery(id+"F8.wireOp",EDGE,"E6.3.1")])]});
            var Q33;
            Q33=makeQuery(id+"F10.opExtrude","SWEPT_EDGE",EDGE,{"disambiguationData":[OSD([sQuery(id+"F8.wireOp",EDGE,"E6.4.1"),sQuery(id+"F8.wireOp",EDGE,"E6.4.2")])]});
            var Q34;
            Q34=makeQuery(id+"F10.opExtrude","SWEPT_EDGE",EDGE,{"disambiguationData":[OSD([sQuery(id+"F8.wireOp",EDGE,"E6.2.0"),sQuery(id+"F8.wireOp",EDGE,"E6.2.1")])]});
            var Q35;
            Q35=makeQuery(id+"F10.opExtrude","SWEPT_EDGE",EDGE,{"disambiguationData":[OSD([sQuery(id+"F8.wireOp",EDGE,"E6.3.1"),sQuery(id+"F8.wireOp",EDGE,"E6.3.2")])]});
            chamfer(context, id + "F21", {"entities" : qUnion([Q0, Q1, Q2, Q3, Q4, Q5, Q6, Q7, Q8, Q9, Q10, Q11, Q12, Q13, Q14, Q15, Q16, Q17, Q18, Q19, Q20, Q21, Q22, Q23, Q24, Q25, Q26, Q27, Q28, Q29, Q30, Q31, Q32, Q33, Q34, Q35]), "width" : ((getVariable(context, 'WALL_OVERLAP')) / 2) * mm, "tangentPropagation" : true});
        }
        {
            var Q0;
            Q0=makeQuery(id+"F7.imprint","IMPRINT",FACE,{"disambiguationData":[TD([[makeQuery(id+"F7.imprint","IMPRINT",EDGE,{"derivedFrom":sQuery(id+"F7.wireOp",EDGE,"E2.3.0")}),-1.0]])]});
            var Q1;
            Q1=makeQuery(id+"F7.imprint","IMPRINT",FACE,{"disambiguationData":[TD([[makeQuery(id+"F7.imprint","IMPRINT",EDGE,{"derivedFrom":sQuery(id+"F7.wireOp",EDGE,"E2.2.0")}),-1.0]])]});
            var Q2;
            Q2=makeQuery(id+"F7.imprint","IMPRINT",FACE,{"disambiguationData":[TD([[makeQuery(id+"F7.imprint","IMPRINT",EDGE,{"derivedFrom":sQuery(id+"F7.wireOp",EDGE,"E2.1.0")}),-1.0]])]});
            var Q3;
            Q3=makeQuery(id+"F7.imprint","IMPRINT",FACE,{"disambiguationData":[TD([[makeQuery(id+"F7.imprint","IMPRINT",EDGE,{"derivedFrom":sQuery(id+"F7.wireOp",EDGE,"E1.0")}),-1.0]])]});
            var Q4;
            Q4=makeQuery(id+"F6.imprint","IMPRINT",FACE,{"disambiguationData":[TD([[makeQuery(id+"F6.imprint","IMPRINT",EDGE,{"derivedFrom":sQuery(id+"F6.wireOp",EDGE,"E0.0")}),-1.0]])]});
            var Q5;
            Q5=makeQuery(id+"F7.imprint","IMPRINT",FACE,{"disambiguationData":[TD([[makeQuery(id+"F7.imprint","IMPRINT",EDGE,{"derivedFrom":sQuery(id+"F7.wireOp",EDGE,"E2.5.0")}),-1.0]])]});
            var Q6;
            Q6=makeQuery(id+"F7.imprint","IMPRINT",FACE,{"disambiguationData":[TD([[makeQuery(id+"F7.imprint","IMPRINT",EDGE,{"derivedFrom":sQuery(id+"F7.wireOp",EDGE,"E2.4.0")}),-1.0]])]});
            extrude(context, id + "F22", {"entities" : qUnion([Q0, Q1, Q2, Q3, Q4, Q5, Q6]), "operationType" : NewBodyOperationType.REMOVE, "depth" : 0.8 * mm, "offsetDistance" : 25 * mm});
        }
    });
